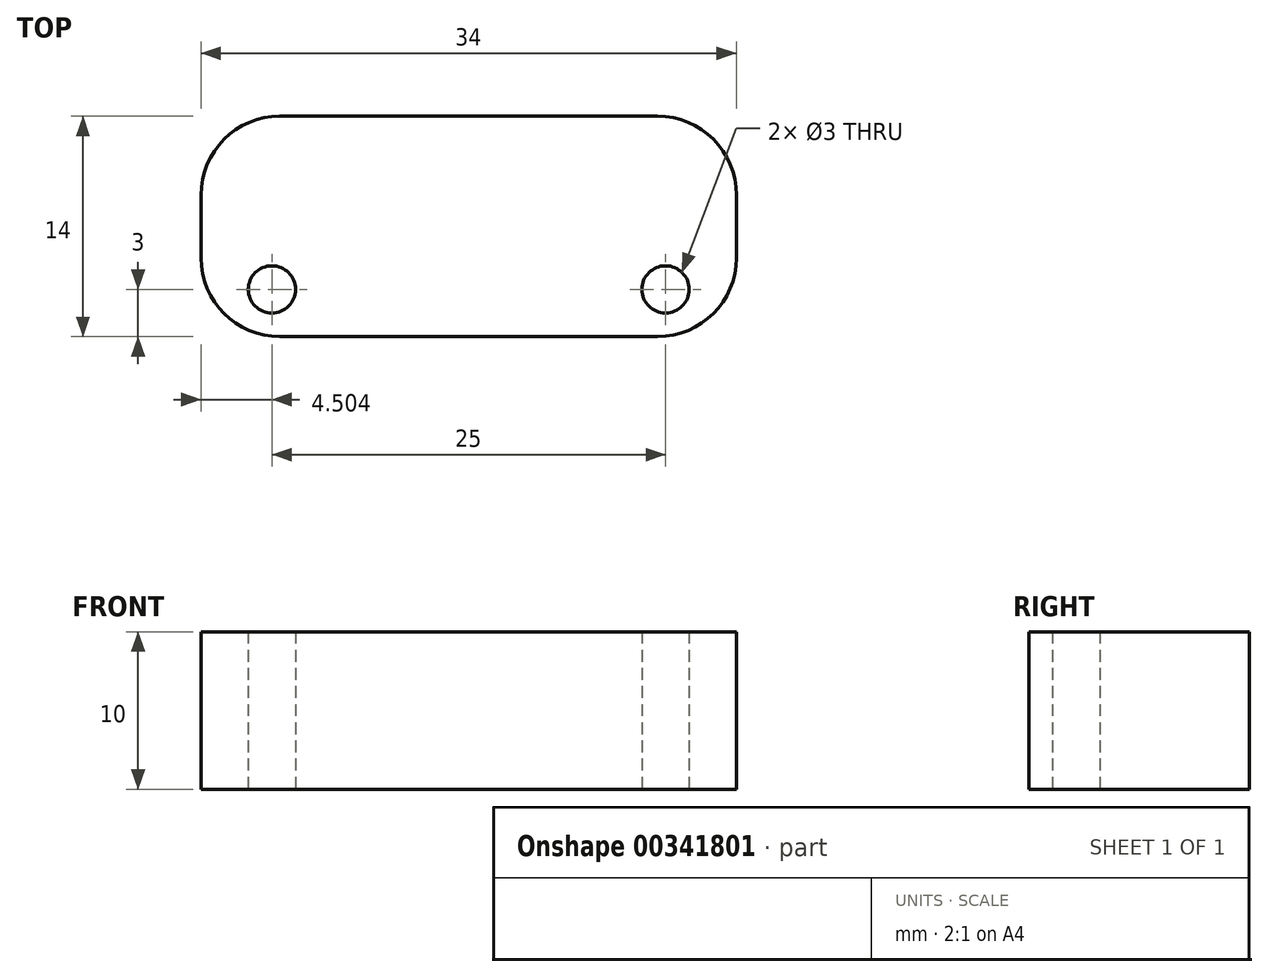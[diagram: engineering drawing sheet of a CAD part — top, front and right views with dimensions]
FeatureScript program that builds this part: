
annotation { "Feature Type Name" : "Feature", "Feature Type Description" : "" }
export const myFeature = defineFeature(function(context is Context, id is Id, definition is map)
    precondition{}
    {
        {
            var Q0;
            Q0=qCreatedBy(makeId("Top.planeOp"),FACE);
            var sketch = newSketch(context, id + "F0", { "sketchPlane" : qUnion([Q0])});
            skLineSegment(sketch, "E0.bottom", {"start": v(-29, 22.81) * mm, "end": v(5, 22.81) * mm});
            skLineSegment(sketch, "E0.top", {"start": v(-29, 8.81) * mm, "end": v(5, 8.81) * mm});
            skLineSegment(sketch, "E0.left", {"start": v(-29, 22.81) * mm, "end": v(-29, 8.81) * mm});
            skLineSegment(sketch, "E0.right", {"start": v(5, 22.81) * mm, "end": v(5, 8.81) * mm});
            skCircle(sketch, "E1", {"center": v(0.5, 11.81) * mm, "radius": 1.5 * mm});
            skCircle(sketch, "E2", {"center": v(-24.5, 11.81) * mm, "radius": 1.5 * mm});
            skSolve(sketch);
        }
        {
            var Q0;
            Q0 = qSketchRegion(id + "F0", true);
            extrude(context, id + "F1", {"entities" : qUnion([Q0]), "depth" : 10 * mm, "offsetDistance" : 25 * mm});
        }
        {
            var Q0;
            Q0=makeQuery(id+"F1.opExtrude","SWEPT_EDGE",EDGE,{"disambiguationData":[OSD([sQuery(id+"F0.wireOp",EDGE,"E0.top"),sQuery(id+"F0.wireOp",EDGE,"E0.right")])]});
            var Q1;
            Q1=makeQuery(id+"F1.opExtrude","SWEPT_EDGE",EDGE,{"disambiguationData":[OSD([sQuery(id+"F0.wireOp",EDGE,"E0.bottom"),sQuery(id+"F0.wireOp",EDGE,"E0.right")])]});
            var Q2;
            Q2=makeQuery(id+"F1.opExtrude","SWEPT_EDGE",EDGE,{"disambiguationData":[OSD([sQuery(id+"F0.wireOp",EDGE,"E0.bottom"),sQuery(id+"F0.wireOp",EDGE,"E0.left")])]});
            var Q3;
            Q3=makeQuery(id+"F1.opExtrude","SWEPT_EDGE",EDGE,{"disambiguationData":[OSD([sQuery(id+"F0.wireOp",EDGE,"E0.top"),sQuery(id+"F0.wireOp",EDGE,"E0.left")])]});
            fillet(context, id + "F2", {"entities" : qUnion([Q0, Q1, Q2, Q3]), "tangentPropagation" : true, "radius" : 5 * mm, "defaultsChanged" : false, "vertexSettings" : [], "allowEdgeOverflow" : false});
        }
    });
